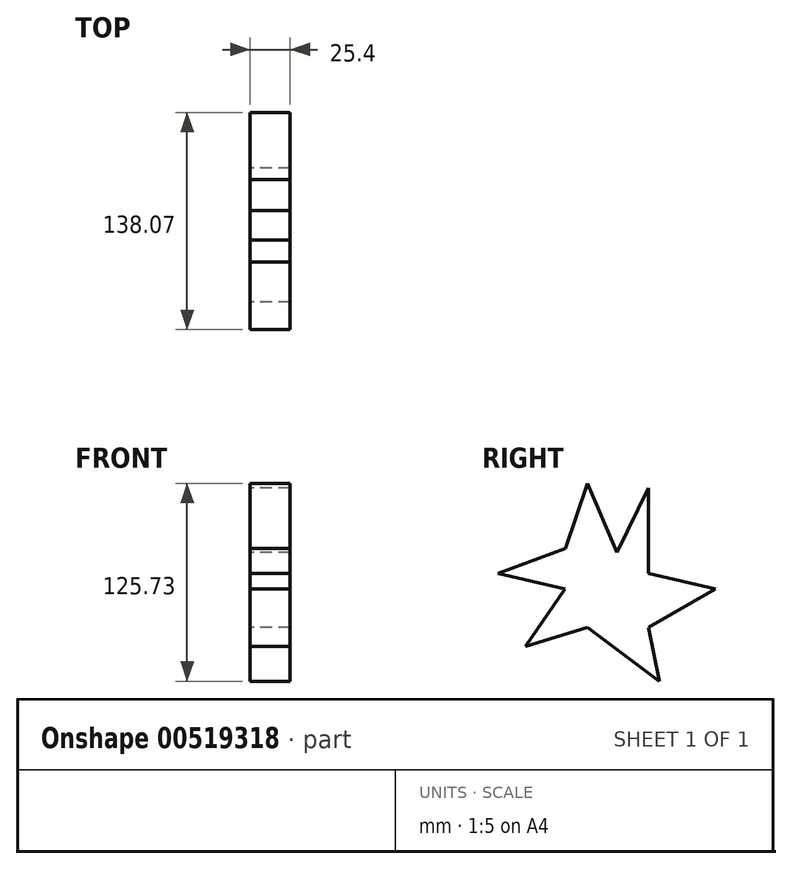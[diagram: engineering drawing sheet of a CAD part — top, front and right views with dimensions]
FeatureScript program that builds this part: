
annotation { "Feature Type Name" : "Feature", "Feature Type Description" : "" }
export const myFeature = defineFeature(function(context is Context, id is Id, definition is map)
    precondition{}
    {
        {
            var Q0;
            Q0=qCreatedBy(makeId("Right.planeOp"),FACE);
            var sketch = newSketch(context, id + "F0", { "sketchPlane" : qUnion([Q0])});
            skLineSegment(sketch, "E0", {"start": v(-42.56, 22.58) * mm, "end": v(-28.59, 63.84) * mm});
            skLineSegment(sketch, "E1", {"start": v(-28.59, 63.84) * mm, "end": v(-9.75, 19.98) * mm});
            skLineSegment(sketch, "E2", {"start": v(-9.75, 19.98) * mm, "end": v(10.07, 60.91) * mm});
            skLineSegment(sketch, "E3", {"start": v(10.07, 60.91) * mm, "end": v(10.07, 6.66) * mm});
            skLineSegment(sketch, "E4", {"start": v(10.07, 6.66) * mm, "end": v(52.63, -3.41) * mm});
            skLineSegment(sketch, "E5", {"start": v(52.63, -3.41) * mm, "end": v(10.07, -27.78) * mm});
            skLineSegment(sketch, "E6", {"start": v(10.07, -27.78) * mm, "end": v(17.22, -61.89) * mm});
            skLineSegment(sketch, "E7", {"start": v(17.22, -61.89) * mm, "end": v(-28.59, -27.78) * mm});
            skLineSegment(sketch, "E8", {"start": v(-28.59, -27.78) * mm, "end": v(-67.9, -39.8) * mm});
            skLineSegment(sketch, "E9", {"start": v(-67.9, -39.8) * mm, "end": v(-42.88, -3.41) * mm});
            skLineSegment(sketch, "E10", {"start": v(-42.88, -3.41) * mm, "end": v(-85.44, 6.66) * mm});
            skLineSegment(sketch, "E11", {"start": v(-85.44, 6.66) * mm, "end": v(-42.56, 22.58) * mm});
            skSolve(sketch);
        }
        {
            var Q0;
            Q0=makeQuery(id+"F0.imprint","IMPRINT",FACE,{"disambiguationData":[TD([[makeQuery(id+"F0.imprint","IMPRINT",EDGE,{"derivedFrom":sQuery(id+"F0.wireOp",EDGE,"E0")}),-1.0]])]});
            extrude(context, id + "F1", {"entities" : qUnion([Q0]), "depth" : 25.4 * mm, "offsetDistance" : 25.4 * mm});
        }
    });
